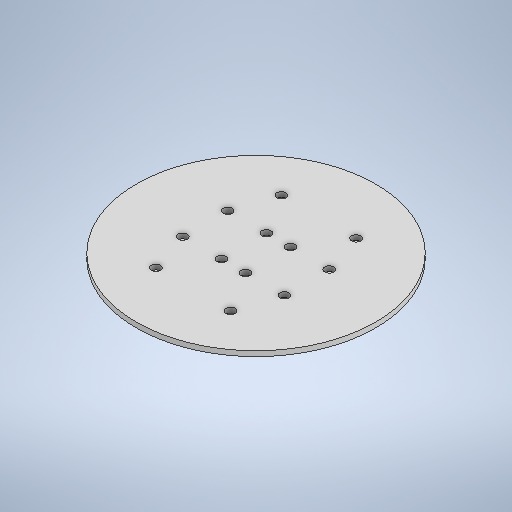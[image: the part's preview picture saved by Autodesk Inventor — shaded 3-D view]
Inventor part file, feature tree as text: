
AUTODESK INVENTOR PART (.ipt)
format: ipt  version: 2025.2 (Build 292293000, 293)  size: 249,344 bytes
history: native  units: mm
features: extrude x1, sketch x1
ambient origin geometry x8: Origin, YZ Plane, XZ Plane, XY Plane, X Axis, Y Axis, Z Axis, Center Point
bodies: Solid1 (feature_tree)
feature tree (2):
  extrude  "Extrusion1"  Depth=1.7mm
  sketch  "Sketch1"  dims[d0=80.0mm d1=3.0mm d2=3.0mm d3=3.0mm d4=4.0mm d5=7.5mm d6=13.0mm d7=0.0mm d8=12.5mm d9=21.0mm d10=1.7mm d11=0.0mm]
